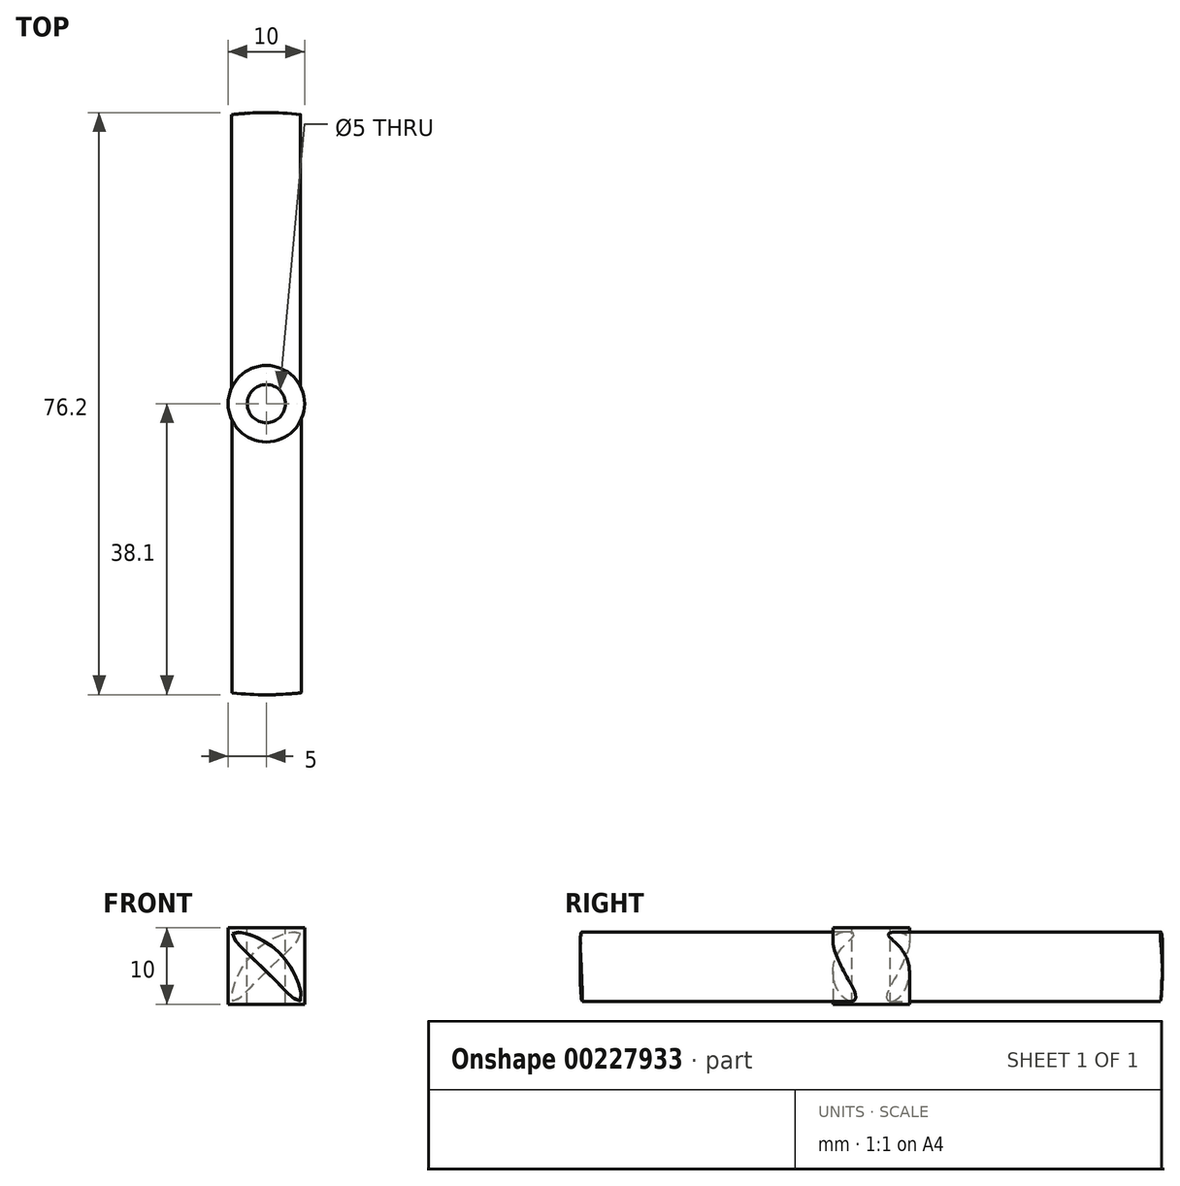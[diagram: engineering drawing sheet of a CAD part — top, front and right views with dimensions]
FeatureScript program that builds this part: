
annotation { "Feature Type Name" : "Feature", "Feature Type Description" : "" }
export const myFeature = defineFeature(function(context is Context, id is Id, definition is map)
    precondition{}
    {
        {
            var Q0;
            Q0=qCreatedBy(makeId("Top.planeOp"),FACE);
            var sketch = newSketch(context, id + "F0", { "sketchPlane" : qUnion([Q0])});
            skCircle(sketch, "E0", {"center": v(0, 0) * mm, "radius": 5 * mm});
            skSolve(sketch);
        }
        {
            var Q0;
            Q0=makeQuery(id+"F0.imprint","IMPRINT",FACE,{"disambiguationData":[TD([[makeQuery(id+"F0.imprint","IMPRINT",EDGE,{"derivedFrom":sQuery(id+"F0.wireOp",EDGE,"E0")}),1.0]])]});
            extrude(context, id + "F1", {"entities" : qUnion([Q0]), "depth" : 10 * mm});
        }
        {
            var Q0;
            Q0=qCreatedBy(makeId("Front.planeOp"),FACE);
            var sketch = newSketch(context, id + "F2", { "sketchPlane" : qUnion([Q0])});
            skFitSpline(sketch, "E1", {"points": [v(-4.43, 9.26) * mm, v(1.62, 6.82) * mm, v(4.45, 0.45) * mm, v(0, 4.28) * mm, v(-4.43, 9.26) * mm]});
            skSolve(sketch);
        }
        {
            var Q0;
            Q0 = qSketchRegion(id + "F2", true);
            extrude(context, id + "F3", {"entities" : qUnion([Q0]), "depth" : 100 * mm});
        }
        {
            var Q0;
            Q0=makeQuery(id+"F3.opExtrude","SWEPT_BODY",BODY,{"disambiguationData":[OSD([sQuery(id+"F2.wireOp",EDGE,"E1")])]});
            var Q1;
            Q1=makeQuery(id+"F1.opExtrude","CAP_EDGE",EDGE,{"disambiguationData":[OSD([sQuery(id+"F0.wireOp",EDGE,"E0")])],"isStart":false});
            circularPattern(context, id + "F4", {"operationType" : NewBodyOperationType.ADD, "entities" : qUnion([Q0]), "axis" : qUnion([Q1]), "angle" : 360 * degree, "instanceCount" : 2, "equalSpace" : true});
        }
        {
            var Q0;
            Q0=makeQuery(id+"F1.opExtrude","CAP_FACE",FACE,{"disambiguationData":[OSD([sQuery(id+"F0.wireOp",EDGE,"E0")])],"isStart":false});
            var sketch = newSketch(context, id + "F5", { "sketchPlane" : qUnion([Q0])});
            skCircle(sketch, "E2", {"center": v(0, 0) * mm, "radius": 38.1 * mm});
            skCircle(sketch, "E3", {"center": v(0, 0) * mm, "radius": 106.33 * mm});
            skCircle(sketch, "E4", {"center": v(0, 0) * mm, "radius": 2.5 * mm});
            skSolve(sketch);
        }
        {
            var Q0;
            Q0=makeQuery(id+"F5.imprint","IMPRINT",FACE,{"disambiguationData":[TD([[makeQuery(id+"F5.imprint","IMPRINT",EDGE,{"derivedFrom":sQuery(id+"F5.wireOp",EDGE,"E2")}),-1.0]])]});
            var Q1;
            Q1=makeQuery(id+"F5.imprint","IMPRINT",FACE,{"disambiguationData":[TD([[makeQuery(id+"F5.imprint","IMPRINT",EDGE,{"derivedFrom":sQuery(id+"F5.wireOp",EDGE,"E4")}),1.0]])]});
            extrude(context, id + "F6", {"entities" : qUnion([Q0, Q1]), "operationType" : NewBodyOperationType.REMOVE, "oppositeDirection" : true, "depth" : 25 * mm});
        }
    });
